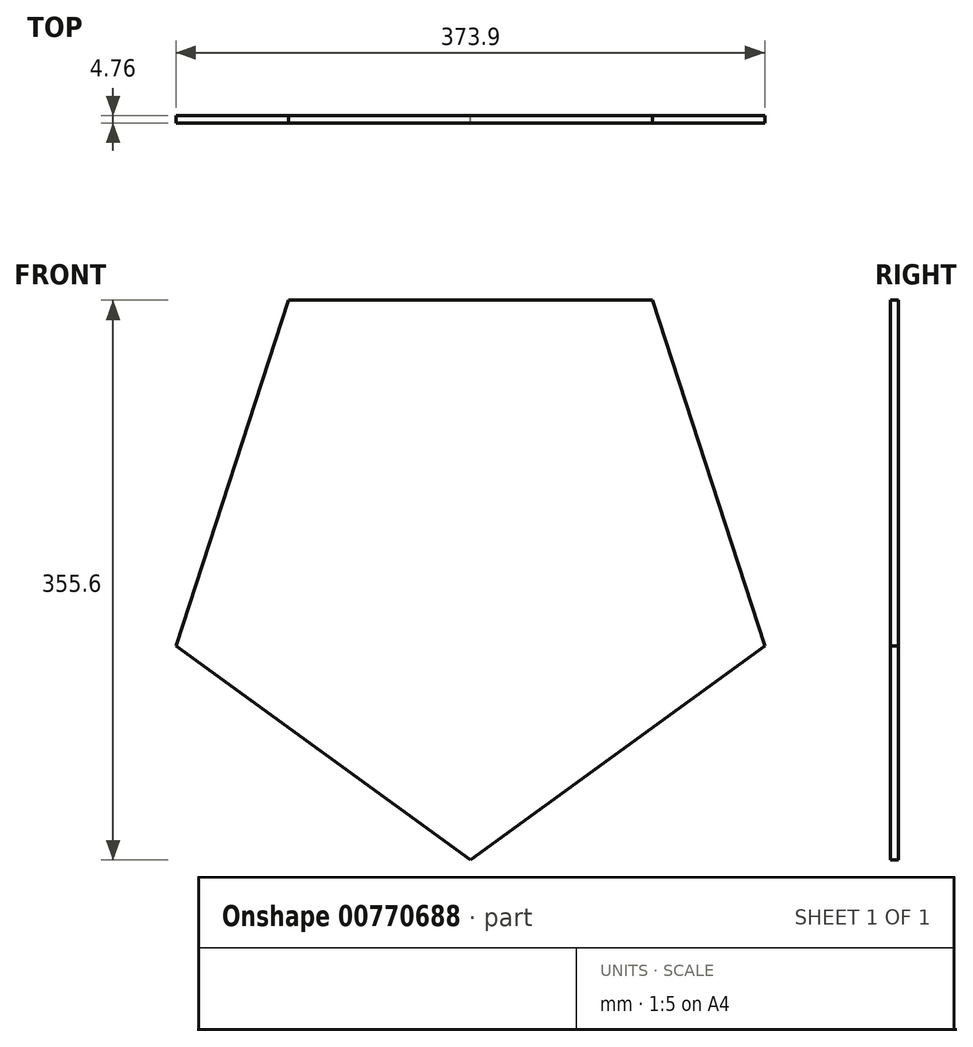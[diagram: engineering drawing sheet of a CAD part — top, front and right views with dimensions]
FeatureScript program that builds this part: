
annotation { "Feature Type Name" : "Feature", "Feature Type Description" : "" }
export const myFeature = defineFeature(function(context is Context, id is Id, definition is map)
    precondition{}
    {
        {
            var Q0;
            Q0=qCreatedBy(makeId("Front.planeOp"),FACE);
            var sketch = newSketch(context, id + "F0", { "sketchPlane" : qUnion([Q0])});
            skCircle(sketch, "E0.cCircle", {"center": v(0, 0) * mm, "radius": 159.03 * mm, "construction": true});
            skLineSegment(sketch, "E0.0", {"start": v(-115.54, 159.03) * mm, "end": v(115.54, 159.03) * mm});
            skLineSegment(sketch, "E0.1", {"start": v(115.54, 159.03) * mm, "end": v(186.95, -60.74) * mm});
            skLineSegment(sketch, "E0.2", {"start": v(186.95, -60.74) * mm, "end": v(0, -196.57) * mm});
            skLineSegment(sketch, "E0.3", {"start": v(0, -196.57) * mm, "end": v(-186.95, -60.74) * mm});
            skLineSegment(sketch, "E0.4", {"start": v(-186.95, -60.74) * mm, "end": v(-115.54, 159.03) * mm});
            skPoint(sketch, "E0.0.midPoint", {"position": v(0, 159.03) * mm});
            skSolve(sketch);
        }
        {
            var Q0;
            Q0=makeQuery(id+"F0.imprint","IMPRINT",FACE,{"disambiguationData":[TD([[makeQuery(id+"F0.imprint","IMPRINT",EDGE,{"derivedFrom":sQuery(id+"F0.wireOp",EDGE,"E0.0")}),-1.0]])]});
            extrude(context, id + "F1", {"entities" : qUnion([Q0]), "endBound" : BoundingType.SYMMETRIC, "depth" : 4.76 * mm, "offsetDistance" : 25.4 * mm});
        }
    });
